# Revit family: XEM4
name_source: partatom
category: Lighting Fixtures
revit_build: Autodesk Revit MEP 2012 (Build: 20110309_2315(x64)
units: mm (PartAtom-declared; Revit-internal decimal feet)

## types (1)
- XEM4
    Apparent Load = 0 VA
    Backbox = Hubbell - White
    Ballast = E - Electronic, T8, Instant Start
    Color Filter = 16777215
    Default Elevation = 48 "
    Description = Enclosed and Gasketed Fiberglass Industrial
    Dimming Lamp Color Temperature Shift = <None>
    Emit Shape Visible in Rendering = No
    Emit from Rectangle Length = 47 "
    Emit from Rectangle Width = 5.5 "
    Glass = Hubbell - White Glass
    Lamp = F32T8
    Lamp Type = 32 - 4',T8: 32, 30, 28, or 25 Watt
    Lens Type = RA - Ribbed Acrylic, Impact Resistant
    Load Classification = Lighting
    Manufacturer = Columbia Lighting
    Manufacturer Fax = 866-898-1065
    Model = XEM4
    Options = GLR/TP
    Photometric Web File = XEM4-232-RA-EU.ies
    Product Documentation Link = http://www.columbialighting.com
    Product Page URL = http://www.columbialighting.com
    Row Length = 48 "
    Tilt Angle = -90.00°
    URL = http://www.columbialighting.com
    Voltage = 120 V
    Wattage Comments = 56W

## geometry (parser evidence)
native form markers: Blend x1, Sweep x5
no freeform markers — native parametric forms only
